# Revit family: INTONO C IN 3.3
name_source: partatom
category: Lighting Fixtures
units: mm (PartAtom-declared; Revit-internal decimal feet)

## family parameters
Always vertical = Yes
Cut with Voids When Loaded = No
Host = Ceiling
Light Source = Yes
OmniClass Number = 23.80.70.11
OmniClass Title = Luminaries for Internal Lighting
Part Type = Normal
Room Calculation Point = Yes
Round Connector Dimension = Use Diameter
Shared = No

## types (4) — shared parameters
Body = L&L _Aluminium low copper
CRI = CRI 80; CRI >90
Code = -
Color Filter = 16777215
Control system = 0/1-10V, ON/OFF, DALI
Cutout dimensions = -
Delivered lumen output = 1392 lm (3000K, 15°, CRI 90), 1674 lm (3000K, 15°, CRI 80)
Description = Ceiling mounted for indoor applications
Dimming Lamp Color Temperature Shift = <None>
Emit from Line Length = 609.6 mm  [stored 2 ft]
Energy efficiency class = A A+ A++
Features = easy installation thanks to 4-point magnetic fastener
Height mm = 100 mm  [stored 0.328084 ft]
Horizontal rotation max = 0.00°
IP = IP40
LED Colour = 2700K, 3000K, 4000K
Length mm = 160 mm  [stored 0.524934 ft]
Lens = L&L_Tempered extra-clear glass
Lumen output at source = 1644 lm (3000K, CRI 90), 1976 lm (3000K, CRI 80)
Manufacturer = L&L Luce&Light
Material = Body in die-cast aluminium, screen in black-serigraphed, tempered, transparent extra-clear glass
Model = Intono C IN 3.3
Mounting = surface mounted (ceiling)
No. and type of led = 2 high power density COB LEDs, 2-step MacAdam, 50 000h L95 B10 (Ta 25°C)
Notes = Version compatible with Google Home or Amazon Echo available on request for voice command control
Power = 20W
Power cables = -
Power supply = 230Vac
Power supply unit = built-in
Tilt Angle = 90.00°
Trim = L&L_Black glass
URL = https://www.lucelight.it
URL Accessories and power supply units = https://www.lucelight.it
URL Catalogue = https://www.lucelight.it
URL DXF = https://www.lucelight.it
URL Description = https://www.lucelight.it
URL General code = https://www.lucelight.it
URL IES Photometric file = https://www.lucelight.it
URL Image = https://www.lucelight.it
URL Technical sheet = -
Vertical rotation max = 0.00°
Weight kg = 1.15 kg
Width mm = 85 mm  [stored 0.278871 ft]
Wiring = -
zero-valued in all types: Default Elevation

## per-type parameters (varying)
| type | Optics | Photometric Web File |
| INTONO C IN 3.3 SS 15° (3000K CRI90 20W 230Vac) | 15° | INTONO C 3.3 SS 15° [3000K CRI90 20W 230Vac].IES |
| INTONO C IN 3.3 MM 20° (3000K CRI90 20W 230Vac) | 20° | INTONO C 3.3 MM 20° [3000K CRI90 20W 230Vac].IES |
| INTONO C IN 3.3 LL 43° (3000K CRI90 20W 230Vac) | 43° | INTONO C 3.3 LL 43° [3000K CRI90 20W 230Vac].IES |
| INTONO C IN 3.3 AA (3000K CRI90 20W 230Vac) | asymmetrical | INTONO C 3.3 AA [3000K CRI90 20W 230Vac].IES |

note: [stored X ft] marks values corroborated as IEEE doubles in the binary element streams (Revit-internal decimal feet)

## geometry (parser evidence)
native form markers: Blend x4, Sweep x5
no freeform markers — native parametric forms only
